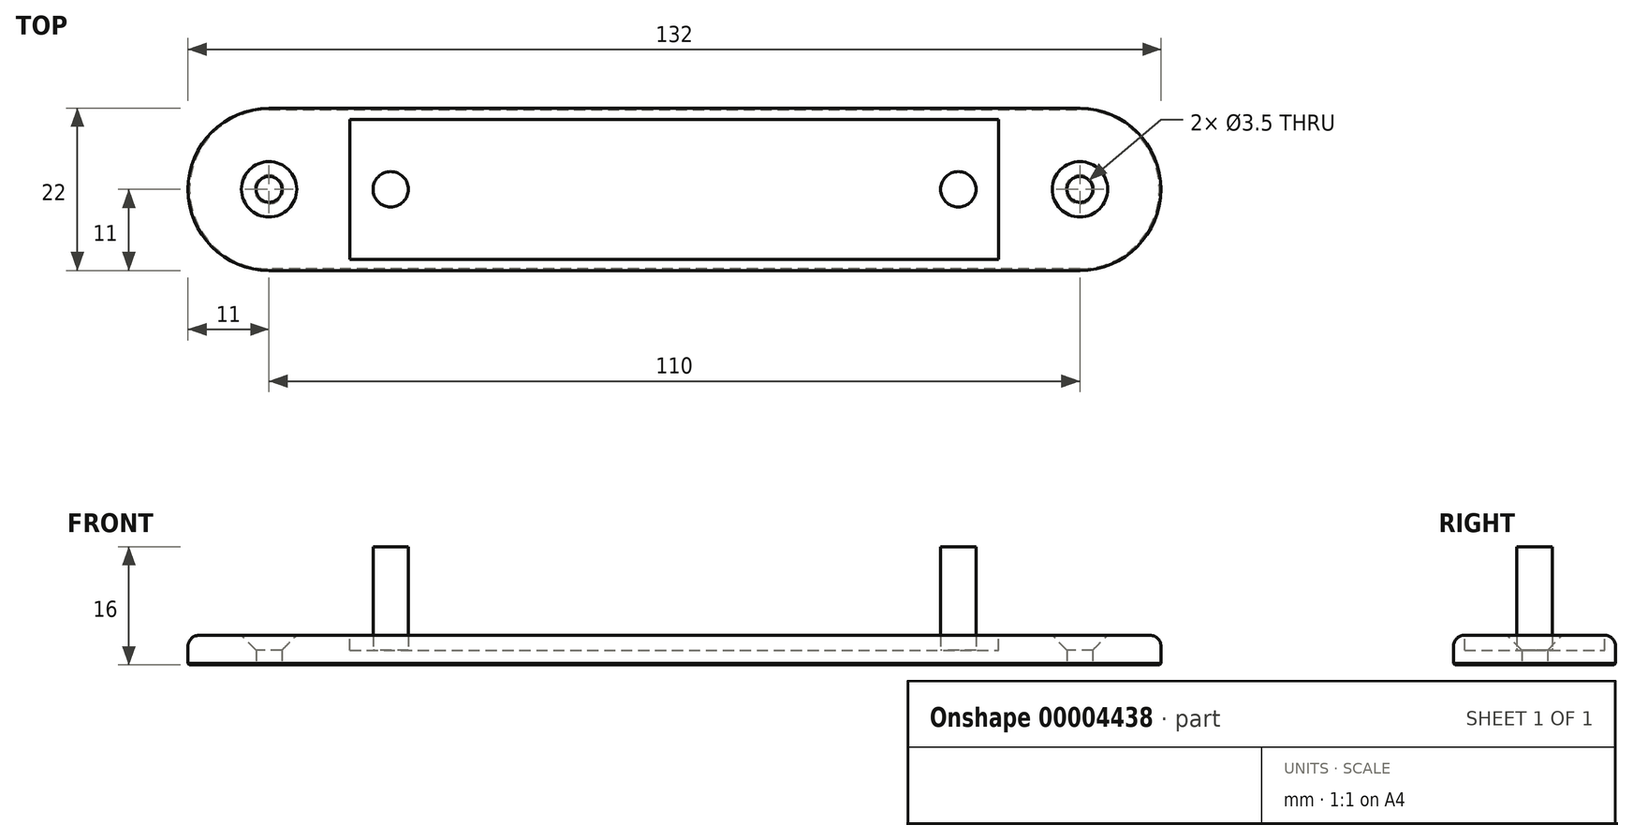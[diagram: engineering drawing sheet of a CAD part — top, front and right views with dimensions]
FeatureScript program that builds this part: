
annotation { "Feature Type Name" : "Feature", "Feature Type Description" : "" }
export const myFeature = defineFeature(function(context is Context, id is Id, definition is map)
    precondition{}
    {
        {
            var Q0;
            Q0=qCreatedBy(makeId("Top.planeOp"),FACE);
            var sketch = newSketch(context, id + "F0", { "sketchPlane" : qUnion([Q0])});
            skLineSegment(sketch, "E0.bottom", {"start": v(0, 0) * mm, "end": v(88, 0) * mm});
            skLineSegment(sketch, "E0.top", {"start": v(0, 19) * mm, "end": v(88, 19) * mm});
            skLineSegment(sketch, "E0.left", {"start": v(0, 0) * mm, "end": v(0, 19) * mm});
            skLineSegment(sketch, "E0.right", {"start": v(88, 0) * mm, "end": v(88, 19) * mm});
            skLineSegment(sketch, "E1.rect.bottom", {"start": v(-10.97, 20.5) * mm, "end": v(99.03, 20.5) * mm});
            skLineSegment(sketch, "E1.rect.top", {"start": v(-10.97, -1.5) * mm, "end": v(99.03, -1.5) * mm});
            skLineSegment(sketch, "E1.rect.left", {"start": v(-10.97, 20.5) * mm, "end": v(-10.97, -1.5) * mm});
            skLineSegment(sketch, "E1.rect.right", {"start": v(99.03, 20.5) * mm, "end": v(99.03, -1.5) * mm});
            skPoint(sketch, "E1.rect.middle", {"position": v(44.03, 9.5) * mm});
            skLineSegment(sketch, "E2", {"start": v(44.03, 9.5) * mm, "end": v(5.53, 9.5) * mm, "construction": true});
            skLineSegment(sketch, "E3", {"start": v(44.03, 9.5) * mm, "end": v(82.53, 9.5) * mm, "construction": true});
            skCircle(sketch, "E4", {"center": v(5.53, 9.5) * mm, "radius": 2.4 * mm, "construction": true});
            skCircle(sketch, "E5", {"center": v(82.53, 9.5) * mm, "radius": 2.4 * mm, "construction": true});
            skLineSegment(sketch, "E6", {"start": v(44.03, 9.5) * mm, "end": v(-10.97, 9.5) * mm, "construction": true});
            skLineSegment(sketch, "E7", {"start": v(44.03, 9.5) * mm, "end": v(99.03, 9.5) * mm, "construction": true});
            skArc(sketch, "E8", {"start": v(-10.97, 20.5) * mm, "mid": v(-21.97, 9.5) * mm, "end": v(-10.97, -1.5) * mm});
            skArc(sketch, "E9", {"start": v(99.03, -1.5) * mm, "mid": v(110.03, 9.5) * mm, "end": v(99.03, 20.5) * mm});
            skCircle(sketch, "E10", {"center": v(99.03, 9.5) * mm, "radius": 1.75 * mm});
            skCircle(sketch, "E11", {"center": v(-10.97, 9.5) * mm, "radius": 1.75 * mm});
            skSolve(sketch);
        }
        {
            var Q0;
            {var subQ4=sQuery(id+"F0.wireOp",EDGE,"E8");Q0=makeQuery(id+"F0.imprint","IMPRINT",FACE,{"disambiguationData":[TD([[makeQuery(id+"F0.imprint","IMPRINT",EDGE,{"derivedFrom":subQ4}),1.0]])]});}
            var Q1;
            {var subQ4=sQuery(id+"F0.wireOp",EDGE,"E9");Q1=makeQuery(id+"F0.imprint","IMPRINT",FACE,{"disambiguationData":[TD([[makeQuery(id+"F0.imprint","IMPRINT",EDGE,{"derivedFrom":subQ4}),1.0]])]});}
            var Q2;
            Q2=makeQuery(id+"F0.imprint","IMPRINT",FACE,{"disambiguationData":[TD([[makeQuery(id+"F0.imprint","IMPRINT",EDGE,{"derivedFrom":sQuery(id+"F0.wireOp",EDGE,"E0.bottom")}),-1.0]])]});
            var Q3;
            Q3=makeQuery(id+"F0.imprint","IMPRINT",FACE,{"disambiguationData":[TD([[makeQuery(id+"F0.imprint","IMPRINT",EDGE,{"derivedFrom":sQuery(id+"F0.wireOp",EDGE,"E0.bottom")}),1.0]])]});
            var Q4;
            Q4=sQuery(id+"F0.wireOp",EDGE,"E9");
            var Q5;
            Q5=sQuery(id+"F0.wireOp",EDGE,"E1.rect.bottom");
            var Q6;
            Q6=sQuery(id+"F0.wireOp",EDGE,"E8");
            var Q7;
            Q7=sQuery(id+"F0.wireOp",EDGE,"E1.rect.top");
            extrude(context, id + "F1", {"entities" : qUnion([Q0, Q1, Q2, Q3]), "surfaceEntities" : qUnion([Q4, Q5, Q6, Q7]), "depth" : 4 * mm});
        }
        {
            var Q0;
            Q0=makeQuery(id+"F1.opExtrude","CAP_FACE",FACE,{"disambiguationData":[OSD([sQuery(id+"F0.wireOp",EDGE,"E1.rect.bottom"),sQuery(id+"F0.wireOp",EDGE,"E1.rect.top"),sQuery(id+"F0.wireOp",EDGE,"E8"),sQuery(id+"F0.wireOp",EDGE,"E9"),sQuery(id+"F0.wireOp",EDGE,"E10"),sQuery(id+"F0.wireOp",EDGE,"E11")])],"isStart":false});
            var sketch = newSketch(context, id + "F2", { "sketchPlane" : qUnion([Q0])});
            skLineSegment(sketch, "E12.0", {"start": v(88, 0) * mm, "end": v(88, 19) * mm});
            skLineSegment(sketch, "E12.1", {"start": v(0, 19) * mm, "end": v(88, 19) * mm});
            skLineSegment(sketch, "E12.2", {"start": v(0, 0) * mm, "end": v(88, 0) * mm});
            skLineSegment(sketch, "E12.3", {"start": v(0, 0) * mm, "end": v(0, 19) * mm});
            skSolve(sketch);
        }
        {
            var Q0;
            Q0=makeQuery(id+"F2.imprint","IMPRINT",FACE,{"disambiguationData":[TD([[makeQuery(id+"F2.imprint","IMPRINT",EDGE,{"derivedFrom":sQuery(id+"F2.wireOp",EDGE,"E12.0")}),1.0]])]});
            var Q1;
            Q1=sQuery(id+"F0.wireOp",EDGE,"E0.bottom");
            var Q2;
            Q2=sQuery(id+"F0.wireOp",EDGE,"E0.left");
            var Q3;
            Q3=sQuery(id+"F0.wireOp",EDGE,"E0.top");
            var Q4;
            Q4=sQuery(id+"F0.wireOp",EDGE,"E0.right");
            extrude(context, id + "F3", {"entities" : qUnion([Q0]), "operationType" : NewBodyOperationType.REMOVE, "surfaceEntities" : qUnion([Q1, Q2, Q3, Q4]), "oppositeDirection" : true, "depth" : 2 * mm});
        }
        {
            var Q0;
            Q0=qCreatedBy(makeId("Top.planeOp"),FACE);
            var sketch = newSketch(context, id + "F4", { "sketchPlane" : qUnion([Q0])});
            skCircle(sketch, "E13.0", {"center": v(5.53, 9.5) * mm, "radius": 2.4 * mm});
            skCircle(sketch, "E13.1", {"center": v(82.53, 9.5) * mm, "radius": 2.4 * mm});
            skSolve(sketch);
        }
        {
            var Q0;
            Q0 = qSketchRegion(id + "F4", true);
            extrude(context, id + "F5", {"entities" : qUnion([Q0]), "operationType" : NewBodyOperationType.ADD, "depth" : 16 * mm});
        }
        {
            var Q0;
            Q0=makeQuery(id+"F1.opExtrude","CAP_EDGE",EDGE,{"disambiguationData":[OSD([sQuery(id+"F0.wireOp",EDGE,"E11")])],"isStart":false});
            chamfer(context, id + "F6", {"entities" : qUnion([Q0]), "width" : 2 * mm});
        }
        {
            var Q0;
            Q0=makeQuery(id+"F1.opExtrude","CAP_EDGE",EDGE,{"disambiguationData":[OSD([sQuery(id+"F0.wireOp",EDGE,"E10")])],"isStart":false});
            chamfer(context, id + "F7", {"entities" : qUnion([Q0]), "width" : 2 * mm, "tangentPropagation" : true});
        }
        {
            var Q0;
            Q0=makeQuery(id+"F1.opExtrude","CAP_EDGE",EDGE,{"disambiguationData":[OSD([sQuery(id+"F0.wireOp",EDGE,"E9")])],"isStart":false});
            var Q1;
            Q1=makeQuery(id+"F1.opExtrude","CAP_EDGE",EDGE,{"disambiguationData":[OSD([sQuery(id+"F0.wireOp",EDGE,"E1.rect.top")])],"isStart":false});
            var Q2;
            Q2=makeQuery(id+"F1.opExtrude","CAP_EDGE",EDGE,{"disambiguationData":[OSD([sQuery(id+"F0.wireOp",EDGE,"E8")])],"isStart":false});
            var Q3;
            Q3=makeQuery(id+"F1.opExtrude","CAP_EDGE",EDGE,{"disambiguationData":[OSD([sQuery(id+"F0.wireOp",EDGE,"E1.rect.bottom")])],"isStart":false});
            fillet(context, id + "F8", {"entities" : qUnion([Q0, Q1, Q2, Q3]), "radius" : 1.5 * mm, "tangentPropagation" : true, "allowEdgeOverflow" : false});
        }
        {
            var Q0;
            Q0=makeQuery(id+"F1.opExtrude","CAP_FACE",FACE,{"disambiguationData":[OSD([sQuery(id+"F0.wireOp",EDGE,"E1.rect.bottom"),sQuery(id+"F0.wireOp",EDGE,"E1.rect.top"),sQuery(id+"F0.wireOp",EDGE,"E8"),sQuery(id+"F0.wireOp",EDGE,"E9"),sQuery(id+"F0.wireOp",EDGE,"E10"),sQuery(id+"F0.wireOp",EDGE,"E11")])],"isStart":true});
            chamfer(context, id + "F9", {"entities" : qUnion([Q0]), "width" : .2 * mm, "tangentPropagation" : true});
        }
    });
